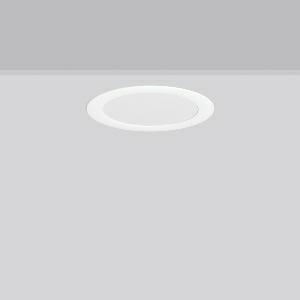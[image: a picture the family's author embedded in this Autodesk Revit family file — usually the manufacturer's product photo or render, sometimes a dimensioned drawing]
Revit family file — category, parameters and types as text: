
# Revit family: toledo_flat_round_672224_002_6616
name_source: partatom
category: Lighting Fixtures
units: mm (PartAtom-declared; Revit-internal decimal feet)

## family parameters
Cut with Voids When Loaded = No
Host = Face
Light Source = No
Part Type = Normal
Room Calculation Point = No
Round Connector Dimension = Use Diameter
Shared = No

## types (1)
- TOLEDO FLAT round (1 x LED Modul 830, 1650 lm, 3000)
    Apparent Load = 17 VA
    Approval mark = CE
    CIE Flux Codes = 48 79 96 100 100
    Color Rendering = 80
    Color Temperature = 3000
    Default Elevation = 1800 mm
    Description = Series: TOLEDO FLAT round
Ultra thin recessed downlight. For escape route illumination. Housing: die-cast aluminium, powder-coated. Lightguide and diffuser made of non-yellowing plastic (PMMA). Diffuser opal matt plastic. Ceiling installation with spring system. Including separate LED converter with connecting cable 250 mm. Self-contained system with automatic self-test. External driver with simple plug-in locking system. 
Colour: white
Diameter: 255 mm
Height: 3 mm
Cut-out diameter: 234 mm
Recess height: 100 mm
Luminaire: recess height: 60-80 mm
Weight: 1.76 kg
Operating mode: maintained power mode
Duration time: 3 h
Lamp: LED
Socket: without socket
Colour temperature: 3000K
Colour rendering index (CRI): 80
System power: 17 W
Rated luminous flux: 1650 lm
Luminous flux, emergency: 450 lm
System power, emergency: -
Control gear: Regulated power supply
Protection class: I
Type of protection: IP 54
    Height = 0 mm  [stored 0 ft]
    Lamp = 1 x LED Modul 830
    Lamp Light Flux = 1650 lm
    Lamp count = 1
    Length = 255 mm
    Lifetime = 50000 h
    Luminous efficacy = 97 lm/W
    Manufacturer = RZB
    ModVariant = No
    Model = 672224.002
    Mounting Place = Ceiling
    Mounting Type = Recessed
    Number of Poles = 1
    OnlyDefault = Yes
    Power Factor = 1
    Product Name = TOLEDO FLAT round
    Product group = Recessed downlights
    ProductGroupID = 402
    Protection Class = Protection class I
    Protection Degree = IP 54
    RLX_Detail_Level = 1
    RLX_Emergency_Light_Flux = 450 lm
    RLX_Emergency_Type = 3
    RLX_Emergency_Type_DB = Yes
    RlxData = <blob elided: 30981 chars, md5=b977881e>
    Socket = socket
    Standby Power = 0 W
    System Light Flux = 1650 lm
    System Power = 17 W
    Type Comments = Product without accessories
    Type Image = 901453.002.jpg
    URL = http://relux.com
    VarID = ---
    Voltage = 0 V
    Weight = 0.00 kg
    Width = 0 mm  [stored 0 ft]

note: [stored X ft] marks values corroborated as IEEE doubles in the binary element streams (Revit-internal decimal feet)

## geometry (parser evidence)
native form markers: Blend x4, Sweep x12
no freeform markers — native parametric forms only
